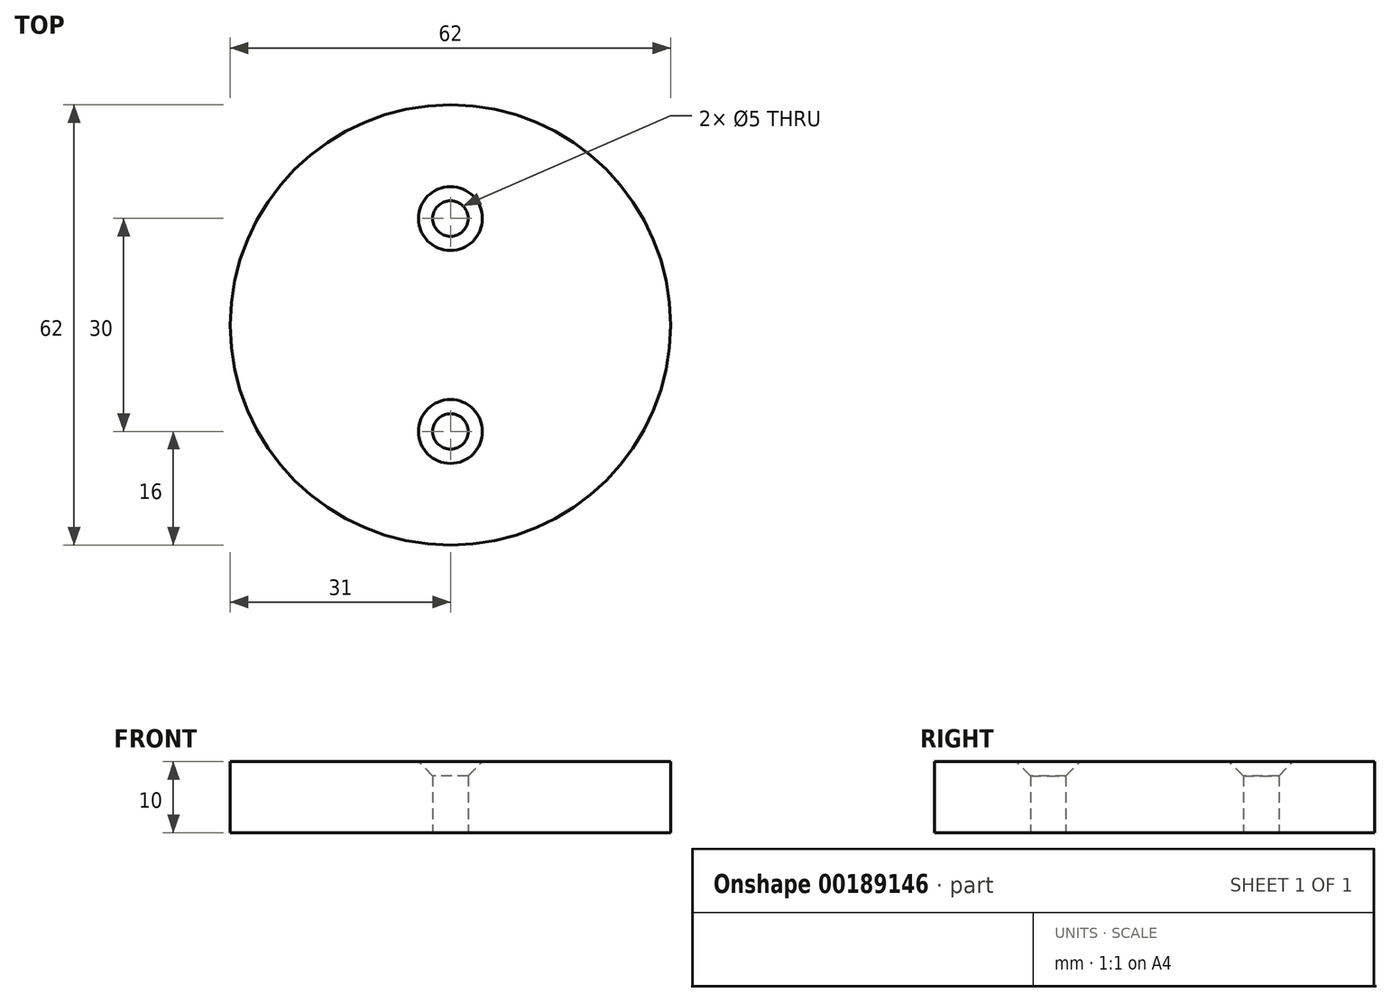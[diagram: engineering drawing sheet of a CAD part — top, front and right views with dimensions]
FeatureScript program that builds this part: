
annotation { "Feature Type Name" : "Feature", "Feature Type Description" : "" }
export const myFeature = defineFeature(function(context is Context, id is Id, definition is map)
    precondition{}
    {
        {
            var Q0;
            Q0=qCreatedBy(makeId("Top.planeOp"),FACE);
            var sketch = newSketch(context, id + "F0", { "sketchPlane" : qUnion([Q0])});
            skCircle(sketch, "E0", {"center": v(0, 0) * mm, "radius": 31 * mm});
            skLineSegment(sketch, "E1", {"start": v(0, 15) * mm, "end": v(23.13, 15) * mm, "construction": true});
            skCircle(sketch, "E2", {"center": v(0, 15) * mm, "radius": 2.5 * mm});
            skCircle(sketch, "E3.MirrorC", {"center": v(0, -15) * mm, "radius": 2.5 * mm});
            skSolve(sketch);
        }
        {
            var Q0;
            Q0=makeQuery(id+"F0.imprint","IMPRINT",FACE,{"disambiguationData":[TD([[makeQuery(id+"F0.imprint","IMPRINT",EDGE,{"derivedFrom":sQuery(id+"F0.wireOp",EDGE,"E0")}),1.0]])]});
            extrude(context, id + "F1", {"entities" : qUnion([Q0]), "depth" : 10 * mm});
        }
        {
            var Q0;
            Q0=makeQuery(id+"F1.opExtrude","CAP_EDGE",EDGE,{"disambiguationData":[OSD([sQuery(id+"F0.wireOp",EDGE,"E2")])],"isStart":false});
            var Q1;
            Q1=makeQuery(id+"F1.opExtrude","CAP_EDGE",EDGE,{"disambiguationData":[OSD([sQuery(id+"F0.wireOp",EDGE,"E3.MirrorC")])],"isStart":false});
            chamfer(context, id + "F2", {"entities" : qUnion([Q0, Q1]), "width" : 2 * mm, "tangentPropagation" : true});
        }
    });
